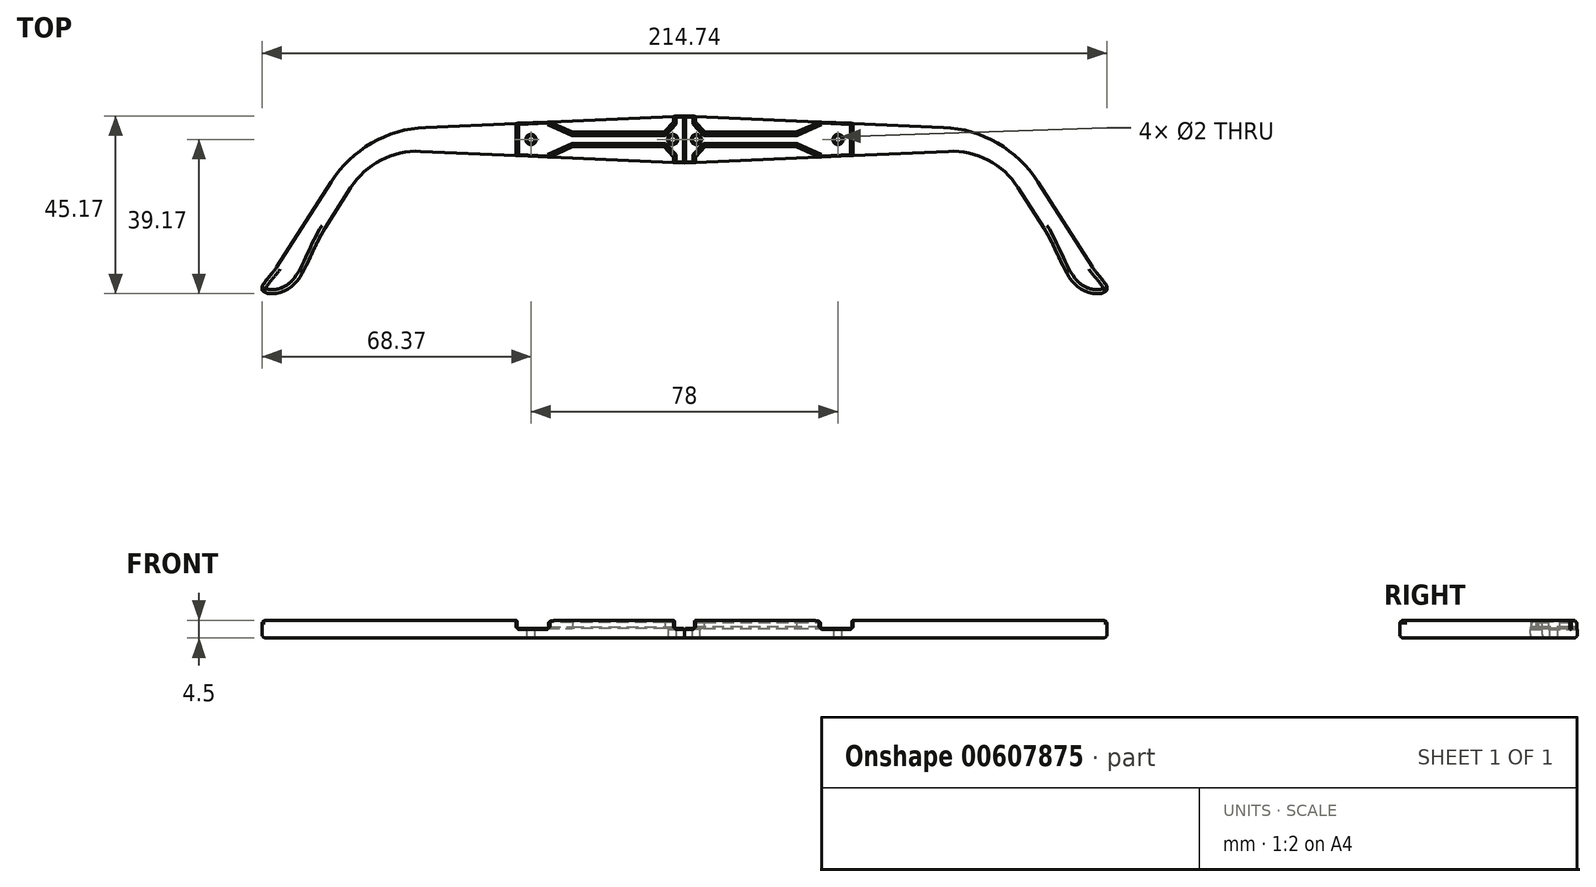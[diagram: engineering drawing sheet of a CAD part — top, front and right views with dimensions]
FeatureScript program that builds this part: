
annotation { "Feature Type Name" : "Feature", "Feature Type Description" : "" }
export const myFeature = defineFeature(function(context is Context, id is Id, definition is map)
    precondition{}
    {
        {
            var Q0;
            Q0=qCreatedBy(makeId("Top.planeOp"),FACE);
            var sketch = newSketch(context, id + "F0", { "sketchPlane" : qUnion([Q0])});
            skLineSegment(sketch, "E0", {"start": v(0, 0) * mm, "end": v(80, 0) * mm});
            skLineSegment(sketch, "E1", {"start": v(0, 0) * mm, "end": v(0, 6) * mm});
            skLineSegment(sketch, "E2", {"start": v(0, 6) * mm, "end": v(78.55, 2.5) * mm});
            skLineSegment(sketch, "E3", {"start": v(81.37, 2.37) * mm, "end": v(103.58, -32.4) * mm});
            skLineSegment(sketch, "E4", {"start": v(80, 0) * mm, "end": v(101.52, -33.72) * mm});
            skLineSegment(sketch, "E5", {"start": v(101.52, -33.72) * mm, "end": v(103.58, -32.4) * mm});
            skLineSegment(sketch, "E6.MirrorCS", {"start": v(0, 0) * mm, "end": v(0, -6) * mm});
            skLineSegment(sketch, "E7.MirrorCS", {"start": v(0, -6) * mm, "end": v(78.55, -2.5) * mm});
            skLineSegment(sketch, "E8", {"start": v(78.55, -2.5) * mm, "end": v(99.36, -35.1) * mm});
            skLineSegment(sketch, "E9", {"start": v(99.36, -35.1) * mm, "end": v(101.52, -33.72) * mm});
            skLineSegment(sketch, "E10", {"start": v(0, -6) * mm, "end": v(2.5, -6) * mm});
            skLineSegment(sketch, "E11", {"start": v(5, -1.35) * mm, "end": v(42.5, -1.35) * mm});
            skLineSegment(sketch, "E12", {"start": v(42.5, -1.35) * mm, "end": v(42.5, 0) * mm});
            skLineSegment(sketch, "E13.MirrorCS", {"start": v(0, 6) * mm, "end": v(2.5, 6) * mm});
            skLineSegment(sketch, "E14.MirrorCS", {"start": v(5, 1.35) * mm, "end": v(42.5, 1.35) * mm});
            skLineSegment(sketch, "E15.MirrorCS", {"start": v(42.5, 1.35) * mm, "end": v(42.5, 0) * mm});
            skLineSegment(sketch, "E16", {"start": v(2.5, -6) * mm, "end": v(2.5, -4) * mm});
            skLineSegment(sketch, "E17", {"start": v(2.5, -4) * mm, "end": v(5, -1.35) * mm});
            skLineSegment(sketch, "E18.MirrorCS", {"start": v(2.5, 6) * mm, "end": v(2.5, 4) * mm});
            skLineSegment(sketch, "E19.MirrorCS", {"start": v(2.5, 4) * mm, "end": v(5, 1.35) * mm});
            skLineSegment(sketch, "E20", {"start": v(42.5, 1.35) * mm, "end": v(42.5, 4) * mm});
            skLineSegment(sketch, "E21", {"start": v(42.5, 4) * mm, "end": v(34.5, 4) * mm});
            skLineSegment(sketch, "E22", {"start": v(34.5, 4) * mm, "end": v(28.5, 1.35) * mm});
            skLineSegment(sketch, "E23.MirrorCS", {"start": v(42.5, -1.35) * mm, "end": v(42.5, -4) * mm});
            skLineSegment(sketch, "E24.MirrorCS", {"start": v(42.5, -4) * mm, "end": v(34.5, -4) * mm});
            skLineSegment(sketch, "E25.MirrorCS", {"start": v(34.5, -4) * mm, "end": v(28.5, -1.35) * mm});
            skCircle(sketch, "E26", {"center": v(3, 0) * mm, "radius": 1 * mm});
            skCircle(sketch, "E27", {"center": v(39, 0) * mm, "radius": 1 * mm});
            skFitSpline(sketch, "E28", {"points": [v(91.29, -22.45) * mm, v(100.77, -38.03) * mm, v(107.33, -38.17) * mm, v(103.58, -32.4) * mm], "startDerivative": vector(25.02, -39.2) * mm, "endDerivative": vector(-12.62, 19.77) * mm});
            skLineSegment(sketch, "E29", {"start": v(104.74, -34.23) * mm, "end": v(103.58, -32.4) * mm, "construction": true});
            skLineSegment(sketch, "E30", {"start": v(78.55, -2.5) * mm, "end": v(80, 0) * mm, "construction": true});
            skLineSegment(sketch, "E31", {"start": v(80, 0) * mm, "end": v(81.37, 2.37) * mm, "construction": true});
            skLineSegment(sketch, "E32", {"start": v(78.55, 2.5) * mm, "end": v(81.37, 2.37) * mm});
            skSolve(sketch);
        }
        {
            var Q0;
            {var subQ9=sQuery(id+"F0.wireOp",EDGE,"E3");Q0=makeQuery(id+"F0.imprint","IMPRINT",FACE,{"disambiguationData":[TD([[makeQuery(id+"F0.imprint","IMPRINT",EDGE,{"derivedFrom":subQ9}),-1.0]])]});}
            var Q1;
            {var subQ4=sQuery(id+"F0.wireOp",EDGE,"E4");Q1=makeQuery(id+"F0.imprint","IMPRINT",FACE,{"disambiguationData":[TD([[makeQuery(id+"F0.imprint","IMPRINT",EDGE,{"derivedFrom":subQ4}),-1.0]])]});}
            var Q2;
            {var subQ2=sQuery(id+"F0.wireOp",EDGE,"E1");Q2=makeQuery(id+"F0.imprint","IMPRINT",FACE,{"disambiguationData":[TD([[makeQuery(id+"F0.imprint","IMPRINT",EDGE,{"derivedFrom":subQ2}),-1.0]])]});}
            var Q3;
            {var subQ7=sQuery(id+"F0.wireOp",EDGE,"E6.MirrorCS");Q3=makeQuery(id+"F0.imprint","IMPRINT",FACE,{"disambiguationData":[TD([[makeQuery(id+"F0.imprint","IMPRINT",EDGE,{"derivedFrom":subQ7}),1.0]])]});}
            var Q4;
            {var subQ0=sQuery(id+"F0.wireOp",EDGE,"E20");Q4=makeQuery(id+"F0.imprint","IMPRINT",FACE,{"disambiguationData":[TD([[makeQuery(id+"F0.imprint","IMPRINT",EDGE,{"derivedFrom":subQ0}),1.0]])]});}
            var Q5;
            {var subQ0=sQuery(id+"F0.wireOp",EDGE,"E23.MirrorCS");Q5=makeQuery(id+"F0.imprint","IMPRINT",FACE,{"disambiguationData":[TD([[makeQuery(id+"F0.imprint","IMPRINT",EDGE,{"derivedFrom":subQ0}),-1.0]])]});}
            var Q6;
            Q6=makeQuery(id+"F0.imprint","IMPRINT",FACE,{"disambiguationData":[TD([[makeQuery(id+"F0.imprint","IMPRINT",EDGE,{"derivedFrom":sQuery(id+"F0.wireOp",EDGE,"E5")}),-1.0]])]});
            extrude(context, id + "F1", {"entities" : qUnion([Q0, Q1, Q2, Q3, Q4, Q5, Q6]), "oppositeDirection" : true, "depth" : 2.5 * mm, "offsetDistance" : 25 * mm});
        }
        {
            var Q0;
            {var subQ9=sQuery(id+"F0.wireOp",EDGE,"E3");Q0=makeQuery(id+"F0.imprint","IMPRINT",FACE,{"disambiguationData":[TD([[makeQuery(id+"F0.imprint","IMPRINT",EDGE,{"derivedFrom":subQ9}),-1.0]])]});}
            var Q1;
            {var subQ4=sQuery(id+"F0.wireOp",EDGE,"E4");Q1=makeQuery(id+"F0.imprint","IMPRINT",FACE,{"disambiguationData":[TD([[makeQuery(id+"F0.imprint","IMPRINT",EDGE,{"derivedFrom":subQ4}),-1.0]])]});}
            var Q2;
            Q2=makeQuery(id+"F0.imprint","IMPRINT",FACE,{"disambiguationData":[TD([[makeQuery(id+"F0.imprint","IMPRINT",EDGE,{"derivedFrom":sQuery(id+"F0.wireOp",EDGE,"E5")}),-1.0]])]});
            extrude(context, id + "F2", {"entities" : qUnion([Q0, Q1, Q2]), "operationType" : NewBodyOperationType.ADD, "depth" : 2 * mm, "offsetDistance" : 25 * mm});
        }
        {
            var Q0;
            {var subQ0=sQuery(id+"F0.wireOp",EDGE,"E8");var subQ1=sQuery(id+"F0.wireOp",EDGE,"E7.MirrorCS");Q0=makeQuery(id+"F2.boolean.opBoolean","MERGE",EDGE,{"derivedFrom":[makeQuery(id+"F1.opExtrude","SWEPT_EDGE",EDGE,{"disambiguationData":[OSD([subQ1,subQ0])]}),makeQuery(id+"F2.opExtrude","SWEPT_EDGE",EDGE,{"disambiguationData":[OSD([subQ1,subQ0])]})]});}
            fillet(context, id + "F3", {"entities" : qUnion([Q0]), "radius" : 20 * mm, "tangentPropagation" : true, "allowEdgeOverflow" : false});
        }
        {
            var Q0;
            {var subQ0=sQuery(id+"F0.wireOp",EDGE,"E3");var subQ1=sQuery(id+"F0.wireOp",EDGE,"E2");Q0=makeQuery(id+"F2.boolean.opBoolean","MERGE",EDGE,{"derivedFrom":[makeQuery(id+"F1.opExtrude","SWEPT_EDGE",EDGE,{"disambiguationData":[OSD([subQ1,subQ0])]}),makeQuery(id+"F2.opExtrude","SWEPT_EDGE",EDGE,{"disambiguationData":[OSD([subQ1,subQ0])]})]});}
            fillet(context, id + "F4", {"entities" : qUnion([Q0]), "radius" : 30 * mm, "tangentPropagation" : true, "allowEdgeOverflow" : false});
        }
        {
            var Q0;
            Q0=makeQuery(id+"F2.opExtrude","CAP_EDGE",EDGE,{"disambiguationData":[OSD([sQuery(id+"F0.wireOp",EDGE,"E7.MirrorCS")])],"isStart":false});
            var Q1;
            Q1=makeQuery(id+"F1.opExtrude","CAP_EDGE",EDGE,{"disambiguationData":[OSD([sQuery(id+"F0.wireOp",EDGE,"E7.MirrorCS")])],"isStart":false});
            fillet(context, id + "F5", {"entities" : qUnion([Q0, Q1]), "radius" : 1 * mm, "tangentPropagation" : true, "allowEdgeOverflow" : false});
        }
        {
            var Q0;
            Q0=makeQuery(id+"F2.opExtrude","SWEPT_FACE",FACE,{"disambiguationData":[OSD([sQuery(id+"F0.wireOp",EDGE,"E21")])]});
            extrude(context, id + "F6", {"entities" : qUnion([Q0]), "operationType" : NewBodyOperationType.REMOVE, "endBound" : BoundingType.SYMMETRIC, "oppositeDirection" : true, "depth" : 25 * mm, "offsetDistance" : 25 * mm});
        }
        {
            var Q0;
            Q0=makeQuery(id+"F6.boolean.opBoolean","MERGE",FACE,{"derivedFrom":[makeQuery(id+"F1.opExtrude","CAP_FACE",FACE,{"disambiguationData":[OSD([sQuery(id+"F0.wireOp",EDGE,"E1"),sQuery(id+"F0.wireOp",EDGE,"E2"),sQuery(id+"F0.wireOp",EDGE,"E3"),sQuery(id+"F0.wireOp",EDGE,"E6.MirrorCS"),sQuery(id+"F0.wireOp",EDGE,"E7.MirrorCS"),sQuery(id+"F0.wireOp",EDGE,"E8"),sQuery(id+"F0.wireOp",EDGE,"E26"),sQuery(id+"F0.wireOp",EDGE,"E27"),sQuery(id+"F0.wireOp",EDGE,"E28"),sQuery(id+"F0.wireOp",EDGE,"E32")])],"isStart":true}),makeQuery(id+"F6.opExtrude","SWEPT_FACE",FACE,{"disambiguationData":[OSD([sQuery(id+"F0.wireOp",EDGE,"E21")])]})]});
            chamfer(context, id + "F7", {"entities" : qUnion([Q0]), "width" : 0.3 * mm, "tangentPropagation" : true});
        }
        {
            var Q0;
            Q0=makeQuery(id+"F2.opExtrude","CAP_EDGE",EDGE,{"disambiguationData":[OSD([sQuery(id+"F0.wireOp",EDGE,"E22")])],"isStart":false});
            var Q1;
            Q1=makeQuery(id+"F2.opExtrude","CAP_EDGE",EDGE,{"disambiguationData":[OSD([sQuery(id+"F0.wireOp",EDGE,"E14.MirrorCS")])],"isStart":false});
            var Q2;
            Q2=makeQuery(id+"F2.opExtrude","CAP_EDGE",EDGE,{"disambiguationData":[OSD([sQuery(id+"F0.wireOp",EDGE,"E11")])],"isStart":false});
            var Q3;
            Q3=makeQuery(id+"F2.opExtrude","CAP_EDGE",EDGE,{"disambiguationData":[OSD([sQuery(id+"F0.wireOp",EDGE,"E25.MirrorCS")])],"isStart":false});
            var Q4;
            Q4=makeQuery(id+"F2.opExtrude","CAP_EDGE",EDGE,{"disambiguationData":[OSD([sQuery(id+"F0.wireOp",EDGE,"E19.MirrorCS")])],"isStart":false});
            var Q5;
            Q5=makeQuery(id+"F2.opExtrude","CAP_EDGE",EDGE,{"disambiguationData":[OSD([sQuery(id+"F0.wireOp",EDGE,"E17")])],"isStart":false});
            chamfer(context, id + "F8", {"entities" : qUnion([Q0, Q1, Q2, Q3, Q4, Q5]), "width" : 0.5 * mm, "tangentPropagation" : true});
        }
        {
            var Q0;
            Q0=makeQuery(id+"F1.opExtrude","SWEPT_BODY",BODY,{"disambiguationData":[OSD([sQuery(id+"F0.wireOp",EDGE,"E1"),sQuery(id+"F0.wireOp",EDGE,"E2"),sQuery(id+"F0.wireOp",EDGE,"E3"),sQuery(id+"F0.wireOp",EDGE,"E6.MirrorCS"),sQuery(id+"F0.wireOp",EDGE,"E7.MirrorCS"),sQuery(id+"F0.wireOp",EDGE,"E8"),sQuery(id+"F0.wireOp",EDGE,"E26"),sQuery(id+"F0.wireOp",EDGE,"E27"),sQuery(id+"F0.wireOp",EDGE,"E28"),sQuery(id+"F0.wireOp",EDGE,"E32")])]});
            var Q1;
            Q1=qCreatedBy(makeId("Right.planeOp"),FACE);
            mirror(context, id + "F9", {"entities" : qUnion([Q0]), "mirrorPlane" : qUnion([Q1])});
        }
    });
